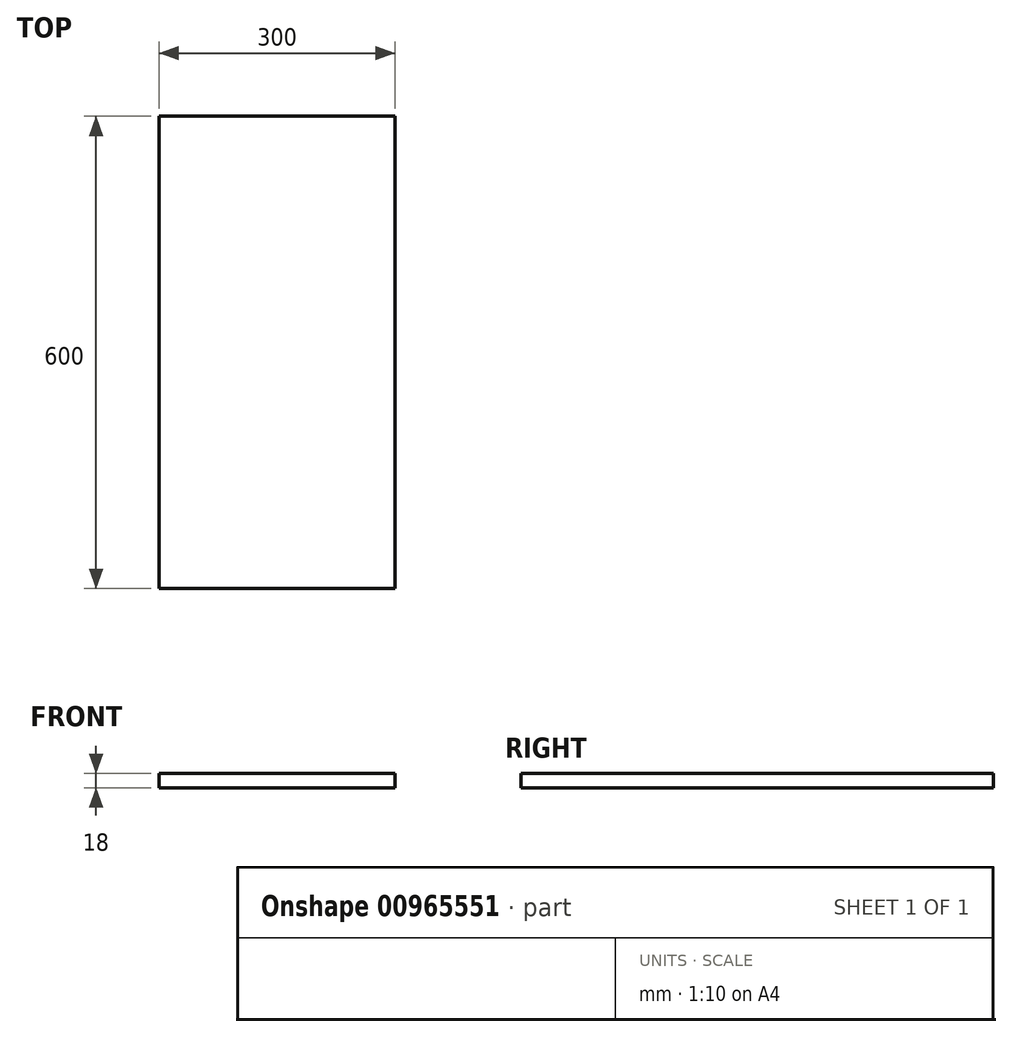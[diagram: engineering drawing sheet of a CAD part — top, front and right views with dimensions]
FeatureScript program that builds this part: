
annotation { "Feature Type Name" : "Feature", "Feature Type Description" : "" }
export const myFeature = defineFeature(function(context is Context, id is Id, definition is map)
    precondition{}
    {
        {
            var Q0;
            Q0=qCreatedBy(makeId("Top.planeOp"),FACE);
            var sketch = newSketch(context, id + "F0", { "sketchPlane" : qUnion([Q0])});
            skLineSegment(sketch, "E0.bottom", {"start": v(150, 300) * mm, "end": v(-150, 300) * mm});
            skLineSegment(sketch, "E0.top", {"start": v(150, -300) * mm, "end": v(-150, -300) * mm});
            skLineSegment(sketch, "E0.left", {"start": v(150, 300) * mm, "end": v(150, -300) * mm});
            skLineSegment(sketch, "E0.right", {"start": v(-150, 300) * mm, "end": v(-150, -300) * mm});
            skPoint(sketch, "E0.middle", {"position": v(0, 0) * mm});
            skSolve(sketch);
        }
        {
            var Q0;
            Q0=makeQuery(id+"F0.imprint","IMPRINT",FACE,{"disambiguationData":[TD([[makeQuery(id+"F0.imprint","IMPRINT",EDGE,{"derivedFrom":sQuery(id+"F0.wireOp",EDGE,"E0.bottom")}),1.0]])]});
            extrude(context, id + "F1", {"entities" : qUnion([Q0]), "depth" : 18 * mm, "offsetDistance" : 25 * mm});
        }
    });
